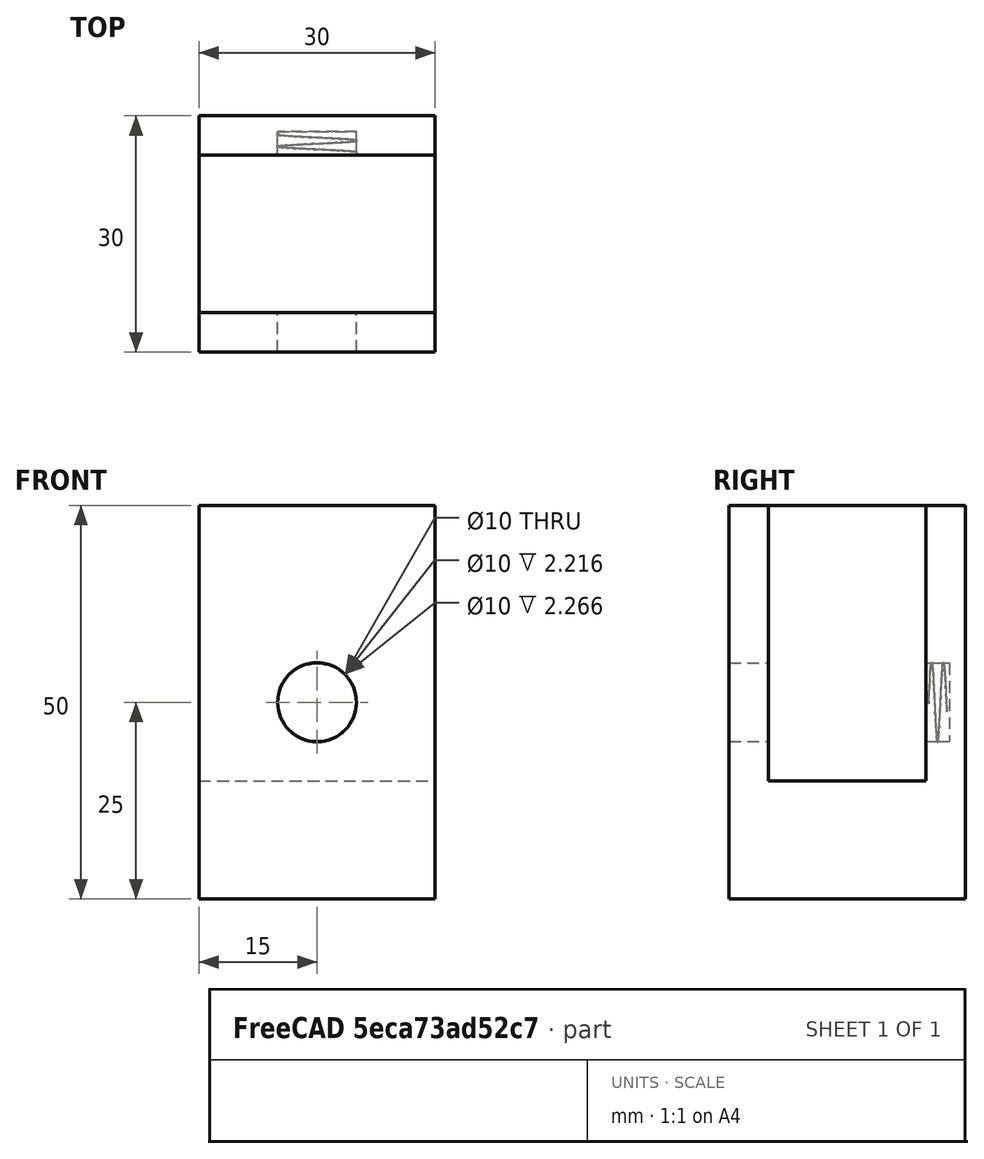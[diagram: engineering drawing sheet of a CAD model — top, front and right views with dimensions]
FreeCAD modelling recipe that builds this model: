
FCSTD DOCUMENT  (FreeCAD 1.2R20251230 (Git shallow))
Label: threaded_clamp_block_body
License: Creative Commons Attribution 4.0
LicenseURL: https://creativecommons.org/licenses/by/4.0/
objects: Part::Feature×4, Part::Cut×3, App::Point×1, Sketcher::SketchObject×1, PartDesign::Pad×1, PartDesign::Body×1
note: 13 computed .brp shape members not serialized (recipe doc carries the construction recipe); baked Part::Feature solids carry a one-line shape summary decoded from their .brp

FEATURE [App::Point] Origin001
  Role = Origin
FEATURE [Sketcher::SketchObject] Sketch_01_Base_X30_Y30
  ArcFitTolerance = 1e-06
  ExternalTypes = [0]
  FullyConstrained = false
  MakeInternals = false
  sketch-geometry (4):
    g0: LineSegment StartX=0 StartY=0 StartZ=0 EndX=30 EndY=0 EndZ=0
    g1: LineSegment StartX=30 StartY=0 StartZ=0 EndX=30 EndY=30 EndZ=0
    g2: LineSegment StartX=30 StartY=30 StartZ=0 EndX=0 EndY=30 EndZ=0
    g3: LineSegment StartX=0 StartY=30 StartZ=0 EndX=0 EndY=0 EndZ=0
  constraints (4):
    c: Coincident(g0,g1)
    c: Coincident(g1,g2)
    c: Coincident(g2,g3)
    c: Coincident(g3,g0)
FEATURE [PartDesign::Pad] Pad_02_Base_Block_Z50
  Direction = (0,0,1)
  Length = 50
  Length2 = 10
  Profile = -> Sketch_01_Base_X30_Y30
  Refine = true
  SideType = 0
  Suppressed = false
  Type = 0
  Type2 = 0
FEATURE [PartDesign::Body] Body_ClampBlock
  AllowCompound = true
  Group = -> [Sketch_01_Base_X30_Y30,Pad_02_Base_Block_Z50]
  Origin = -> Origin
  Tip = -> Pad_02_Base_Block_Z50
FEATURE [Part::Feature] _03_Base_Block_30x30x50
  shape: bbox 30 x 30 x 50 mm, 6 faces (baked)
FEATURE [Part::Feature] _04_Tool_Side_Rectangular_Slot_Through_XZ
  shape: bbox 32 x 20 x 36 mm, 6 faces (baked)
FEATURE [Part::Cut] _05_Cut_Side_Rectangular_Slot_Through_XZ
  Base = -> _03_Base_Block_30x30x50
  Refine = true
  Tool = -> _04_Tool_Side_Rectangular_Slot_Through_XZ
FEATURE [Part::Feature] _06_Tool_Y_Axis_Hole_D10_Depth28
  shape: bbox 10 x 28 x 10 mm, 3 faces (baked)
FEATURE [Part::Cut] _07_Cut_Blind_Hole_Not_Through_Back
  Base = -> _05_Cut_Side_Rectangular_Slot_Through_XZ
  Refine = true
  Tool = -> _06_Tool_Y_Axis_Hole_D10_Depth28
FEATURE [Part::Feature] _08_Tool_Internal_Thread_Groove
  shape: bbox 10.24 x 2.3 x 10.22 mm, 50 faces (baked)
FEATURE [Part::Cut] _09_Cut_Internal_Thread_Groove  label="Final_ThreadedClampBlock"
  Base = -> _07_Cut_Blind_Hole_Not_Through_Back
  Refine = true
  Tool = -> _08_Tool_Internal_Thread_Groove
